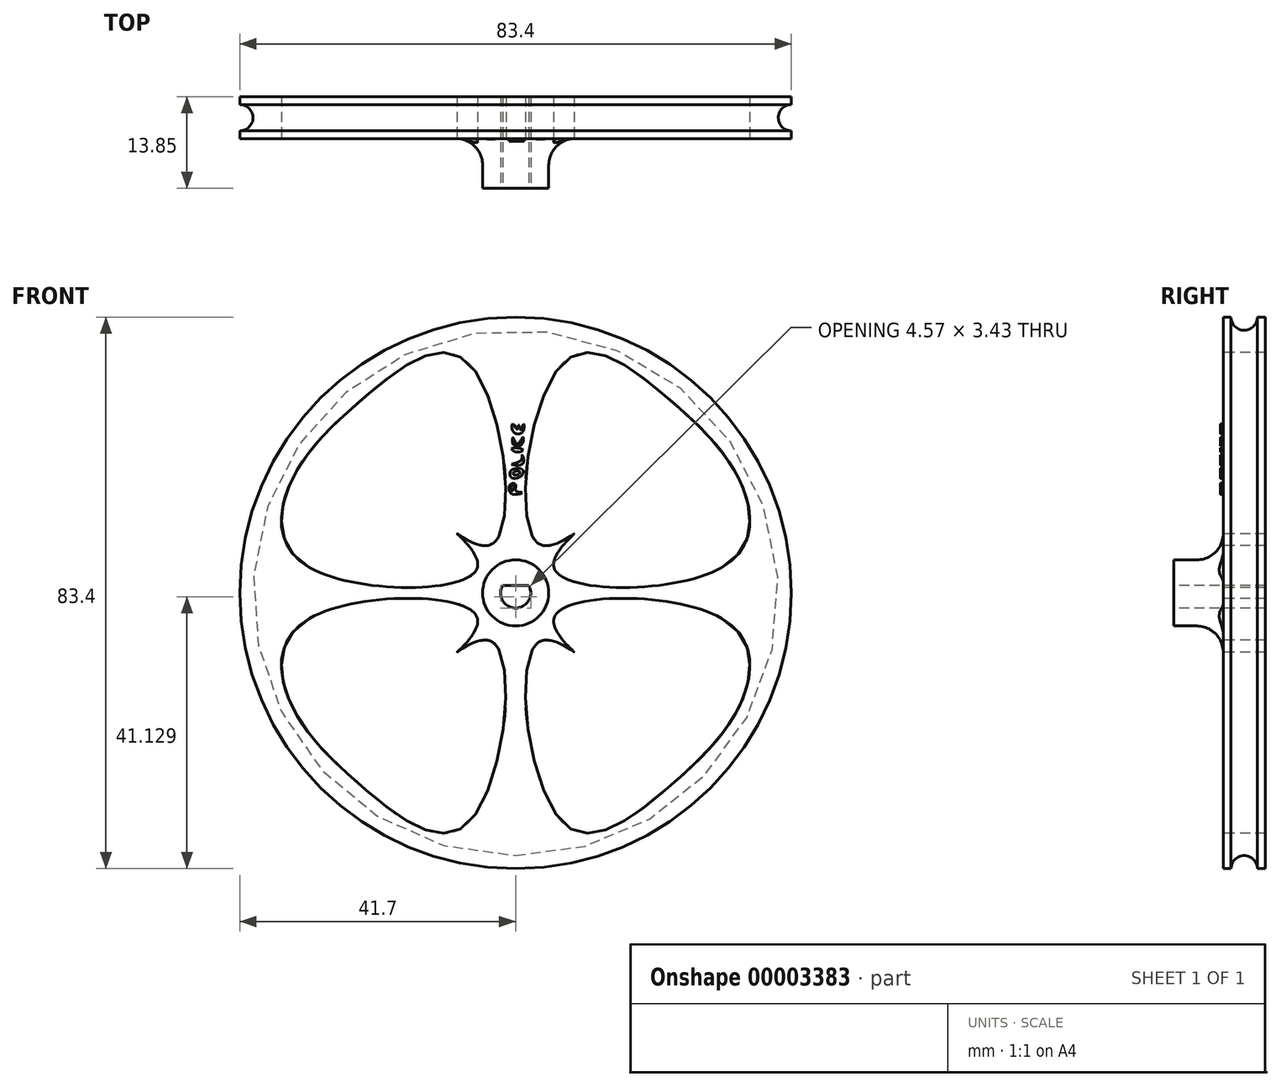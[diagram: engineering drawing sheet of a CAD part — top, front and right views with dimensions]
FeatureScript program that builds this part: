
annotation { "Feature Type Name" : "Feature", "Feature Type Description" : "" }
export const myFeature = defineFeature(function(context is Context, id is Id, definition is map)
    precondition{}
    {
        {
            var Q0;
            Q0=qCreatedBy(makeId("Front.planeOp"),FACE);
            var sketch = newSketch(context, id + "F0", { "sketchPlane" : qUnion([Q0])});
            skArc(sketch, "E0", {"start": v(47.5, 0) * mm, "mid": v(33.59, 33.59) * mm, "end": v(0, 47.5) * mm});
            skLineSegment(sketch, "E1", {"start": v(0, 57.3) * mm, "end": v(0, -52.25) * mm});
            skLineSegment(sketch, "E2", {"start": v(47.5, 0) * mm, "end": v(0, 0) * mm});
            skCircle(sketch, "E3", {"center": v(0, 0) * mm, "radius": 5 * mm});
            skArc(sketch, "E4.0.MirrorCS", {"start": v(-47.5, 0) * mm, "mid": v(-33.59, 33.59) * mm, "end": v(0, 47.5) * mm});
            skArc(sketch, "E5.0.MirrorCS", {"start": v(-47.5, 0) * mm, "mid": v(-33.59, -33.59) * mm, "end": v(0, -47.5) * mm});
            skArc(sketch, "E6.0.MirrorCS", {"start": v(47.5, 0) * mm, "mid": v(33.59, -33.59) * mm, "end": v(0, -47.5) * mm});
            skFitSpline(sketch, "E7", {"points": [v(31.2, 3.87) * mm, v(34.37, 15.91) * mm, v(22.47, 29.91) * mm, v(7.25, 34.85) * mm, v(3.7, 7.34) * mm, v(8.84, 8.95) * mm, v(5.76, 3.96) * mm, v(31.2, 3.87) * mm]});
            skFitSpline(sketch, "E8.0.MirrorC", {"points": [v(-31.2, 3.87) * mm, v(-34.37, 15.91) * mm, v(-22.47, 29.91) * mm, v(-7.25, 34.85) * mm, v(-3.7, 7.34) * mm, v(-8.84, 8.95) * mm, v(-5.76, 3.96) * mm, v(-31.2, 3.87) * mm]});
            skFitSpline(sketch, "E9.0.MirrorC", {"points": [v(31.2, -3.87) * mm, v(34.37, -15.91) * mm, v(22.47, -29.91) * mm, v(7.25, -34.85) * mm, v(3.7, -7.34) * mm, v(8.84, -8.95) * mm, v(5.76, -3.96) * mm, v(31.2, -3.87) * mm]});
            skFitSpline(sketch, "E10.0.MirrorC", {"points": [v(-31.2, -3.87) * mm, v(-34.37, -15.91) * mm, v(-22.47, -29.91) * mm, v(-7.25, -34.85) * mm, v(-3.7, -7.34) * mm, v(-8.84, -8.95) * mm, v(-5.76, -3.96) * mm, v(-31.2, -3.87) * mm]});
            skSolve(sketch);
        }
        {
            var Q0;
            Q0=qCreatedBy(makeId("Right.planeOp"),FACE);
            var sketch = newSketch(context, id + "F1", { "sketchPlane" : qUnion([Q0])});
            skLineSegment(sketch, "E11.bottom", {"start": v(-4.73, 0) * mm, "end": v(4.27, 0) * mm});
            skLineSegment(sketch, "E12", {"start": v(-59.3, 0) * mm, "end": v(49.88, 0) * mm});
            skPoint(sketch, "E13.orphan", {"position": v(0, 42.5) * mm});
            skLineSegment(sketch, "E14", {"start": v(-4.27, 0) * mm, "end": v(-4.27, 0) * mm});
            skLineSegment(sketch, "E15", {"start": v(4.85, 41.7) * mm, "end": v(4.85, 0) * mm});
            skLineSegment(sketch, "E16", {"start": v(-1.5, 41.7) * mm, "end": v(-1.5, 5) * mm});
            skLineSegment(sketch, "E17.bottom", {"start": v(-3.31, 0) * mm, "end": v(3.28, 0) * mm});
            skLineSegment(sketch, "E18.bottom", {"start": v(-9, 5) * mm, "end": v(-1.5, 5) * mm});
            skLineSegment(sketch, "E18.top", {"start": v(-9, 0) * mm, "end": v(0, 0) * mm});
            skLineSegment(sketch, "E18.left", {"start": v(-9, 5) * mm, "end": v(-9, 0) * mm});
            skLineSegment(sketch, "E19", {"start": v(4.85, 41.7) * mm, "end": v(3.66, 41.7) * mm});
            skArc(sketch, "E20", {"start": v(-0.3, 41.7) * mm, "mid": v(1.68, 39.72) * mm, "end": v(3.66, 41.7) * mm});
            skLineSegment(sketch, "E21.trimOffspring", {"start": v(-0.3, 41.7) * mm, "end": v(-1.5, 41.7) * mm});
            skSolve(sketch);
        }
        {
            var Q0;
            {var subQ5=sQuery(id+"F1.wireOp",EDGE,"747c0ea4-b0eb-48b7-bcdc-3955b66142202");Q0=makeQuery(id+"F1.imprint","IMPRINT",FACE,{"disambiguationData":[TD([[makeQuery(id+"F1.imprint","IMPRINT",EDGE,{"derivedFrom":subQ5}),-1.0]])]});}
            var Q1;
            Q1=makeQuery(id+"F1.imprint","IMPRINT",FACE,{"disambiguationData":[TD([[makeQuery(id+"F1.imprint","IMPRINT",EDGE,{"derivedFrom":sQuery(id+"F1.wireOp",EDGE,"E15")}),-1.0]])]});
            var Q2;
            Q2=sQuery(id+"F1.wireOp",EDGE,"E12");
            revolve(context, id + "F2", {"entities" : qUnion([Q0, Q1]), "axis" : qUnion([Q2]), "revolveType" : RevolveType.FULL});
        }
        {
            var Q0;
            Q0=makeQuery(id+"F2.opRevolve","SWEPT_FACE",FACE,{"disambiguationData":[OSD([sQuery(id+"F1.wireOp",EDGE,"E18.left")])]});
            var sketch = newSketch(context, id + "F3", { "sketchPlane" : qUnion([Q0])});
            skArc(sketch, "E22", {"start": v(-1.98, 1.14) * mm, "mid": v(0, -2.29) * mm, "end": v(1.98, 1.14) * mm});
            skLineSegment(sketch, "E23", {"start": v(-1.98, 1.14) * mm, "end": v(1.98, 1.14) * mm});
            skSolve(sketch);
        }
        {
            var Q0;
            Q0=makeQuery(id+"F3.imprint","IMPRINT",FACE,{"disambiguationData":[TD([[makeQuery(id+"F3.imprint","IMPRINT",EDGE,{"derivedFrom":sQuery(id+"F3.wireOp",EDGE,"E22")}),1.0]])]});
            extrude(context, id + "F4", {"entities" : qUnion([Q0]), "operationType" : NewBodyOperationType.REMOVE, "oppositeDirection" : true, "depth" : 25 * mm});
        }
        {
            var Q0;
            Q0=qCreatedBy(makeId("Front.planeOp"),FACE);
            cPlane(context, id + "F5", {"entities" : qUnion([Q0]), "cplaneType" : CPlaneType.OFFSET, "offset" : 1.5 * mm, "width" : 150 * mm, "height" : 150 * mm});
        }
        {
            var Q0;
            Q0=qCreatedBy(id+"F5.planeOp",FACE);
            var sketch = newSketch(context, id + "F6", { "sketchPlane" : qUnion([Q0])});
            skFitSpline(sketch, "E24", {"points": [v(0.98, 15.18) * mm, v(-0.64, 15) * mm, v(-0.75, 16.48) * mm, v(0, 16.34) * mm, v(0, 15.42) * mm, v(0.98, 15.18) * mm]});
            skFitSpline(sketch, "E25", {"points": [v(0.98, 17.83) * mm, v(-0.6, 17.4) * mm, v(-0.71, 18.5) * mm, v(0.98, 18.7) * mm, v(0.98, 17.83) * mm]});
            skFitSpline(sketch, "E26", {"points": [v(0, 18.43) * mm, v(-0.4, 18) * mm, v(0, 17.83) * mm, v(0.7, 18.18) * mm, v(0, 18.43) * mm]});
            skFitSpline(sketch, "E27", {"points": [v(-0.64, 19.45) * mm, v(1.12, 19.6) * mm, v(0.98, 20.86) * mm, v(0.8, 20.05) * mm, v(-0.64, 19.45) * mm]});
            skFitSpline(sketch, "E28", {"points": [v(-0.6, 16.27) * mm, v(-0.6, 15.42) * mm, v(-0.26, 15.97) * mm, v(-0.6, 16.27) * mm]});
            skFitSpline(sketch, "E29", {"points": [v(-0.6, 21.8) * mm, v(0.16, 21.3) * mm, v(1.09, 21.62) * mm, v(0.32, 21.91) * mm, v(-0.6, 21.8) * mm]});
            skFitSpline(sketch, "E30", {"points": [v(-0.44, 23.5) * mm, v(-0.32, 22.49) * mm, v(1.01, 22.55) * mm, v(1.09, 23.56) * mm, v(0.65, 22.79) * mm, v(0, 22.69) * mm, v(-0.44, 23.5) * mm]});
            skFitSpline(sketch, "E31", {"points": [v(-0.4, 25.54) * mm, v(-0.4, 24.41) * mm, v(1.1, 24.37) * mm, v(1.19, 25.5) * mm, v(0.8, 24.63) * mm, v(0.47, 25.4) * mm, v(0.26, 24.73) * mm, v(-0.4, 25.54) * mm]});
            skSolve(sketch);
        }
        {
            var Q0;
            Q0=makeQuery(id+"F6.imprint","IMPRINT",FACE,{"disambiguationData":[TD([[makeQuery(id+"F6.imprint","IMPRINT",EDGE,{"derivedFrom":sQuery(id+"F6.wireOp",EDGE,"E24")}),-1.0]])]});
            var Q1;
            Q1=makeQuery(id+"F6.imprint","IMPRINT",FACE,{"disambiguationData":[TD([[makeQuery(id+"F6.imprint","IMPRINT",EDGE,{"derivedFrom":sQuery(id+"F6.wireOp",EDGE,"E25")}),-1.0]])]});
            var Q2;
            Q2=makeQuery(id+"F6.imprint","IMPRINT",FACE,{"disambiguationData":[TD([[makeQuery(id+"F6.imprint","IMPRINT",EDGE,{"derivedFrom":sQuery(id+"F6.wireOp",EDGE,"E27")}),1.0]])]});
            var Q3;
            Q3=makeQuery(id+"F6.imprint","IMPRINT",FACE,{"disambiguationData":[TD([[makeQuery(id+"F6.imprint","IMPRINT",EDGE,{"derivedFrom":sQuery(id+"F6.wireOp",EDGE,"E29")}),1.0]])]});
            var Q4;
            Q4=makeQuery(id+"F6.imprint","IMPRINT",FACE,{"disambiguationData":[TD([[makeQuery(id+"F6.imprint","IMPRINT",EDGE,{"derivedFrom":sQuery(id+"F6.wireOp",EDGE,"E31")}),1.0]])]});
            var Q5;
            Q5=makeQuery(id+"F6.imprint","IMPRINT",FACE,{"disambiguationData":[TD([[makeQuery(id+"F6.imprint","IMPRINT",EDGE,{"derivedFrom":sQuery(id+"F6.wireOp",EDGE,"E30")}),1.0]])]});
            extrude(context, id + "F7", {"entities" : qUnion([Q0, Q1, Q2, Q3, Q4, Q5]), "operationType" : NewBodyOperationType.ADD, "depth" : 0.4 * mm});
        }
        {
            var Q0;
            Q0=makeQuery(id+"F2.opRevolve","SWEPT_EDGE",EDGE,{"disambiguationData":[OSD([sQuery(id+"F1.wireOp",EDGE,"E16"),sQuery(id+"F1.wireOp",EDGE,"E18.bottom")])]});
            fillet(context, id + "F8", {"entities" : qUnion([Q0]), "radius" : 4 * mm, "tangentPropagation" : true, "allowEdgeOverflow" : false});
        }
        {
            var Q0;
            Q0=makeQuery(id+"F0.imprint","IMPRINT",FACE,{"disambiguationData":[TD([[makeQuery(id+"F0.imprint","IMPRINT",EDGE,{"derivedFrom":sQuery(id+"F0.wireOp",EDGE,"E8.0.MirrorC")}),-1.0]])]});
            var Q1;
            Q1=makeQuery(id+"F0.imprint","IMPRINT",FACE,{"disambiguationData":[TD([[makeQuery(id+"F0.imprint","IMPRINT",EDGE,{"derivedFrom":sQuery(id+"F0.wireOp",EDGE,"E7")}),1.0]])]});
            var Q2;
            Q2=makeQuery(id+"F0.imprint","IMPRINT",FACE,{"disambiguationData":[TD([[makeQuery(id+"F0.imprint","IMPRINT",EDGE,{"derivedFrom":sQuery(id+"F0.wireOp",EDGE,"E9.0.MirrorC")}),-1.0]])]});
            var Q3;
            Q3=makeQuery(id+"F0.imprint","IMPRINT",FACE,{"disambiguationData":[TD([[makeQuery(id+"F0.imprint","IMPRINT",EDGE,{"derivedFrom":sQuery(id+"F0.wireOp",EDGE,"E10.0.MirrorC")}),1.0]])]});
            extrude(context, id + "F9", {"entities" : qUnion([Q0, Q1, Q2, Q3]), "operationType" : NewBodyOperationType.REMOVE, "oppositeDirection" : true, "depth" : 25 * mm, "symmetric" : true});
        }
    });
